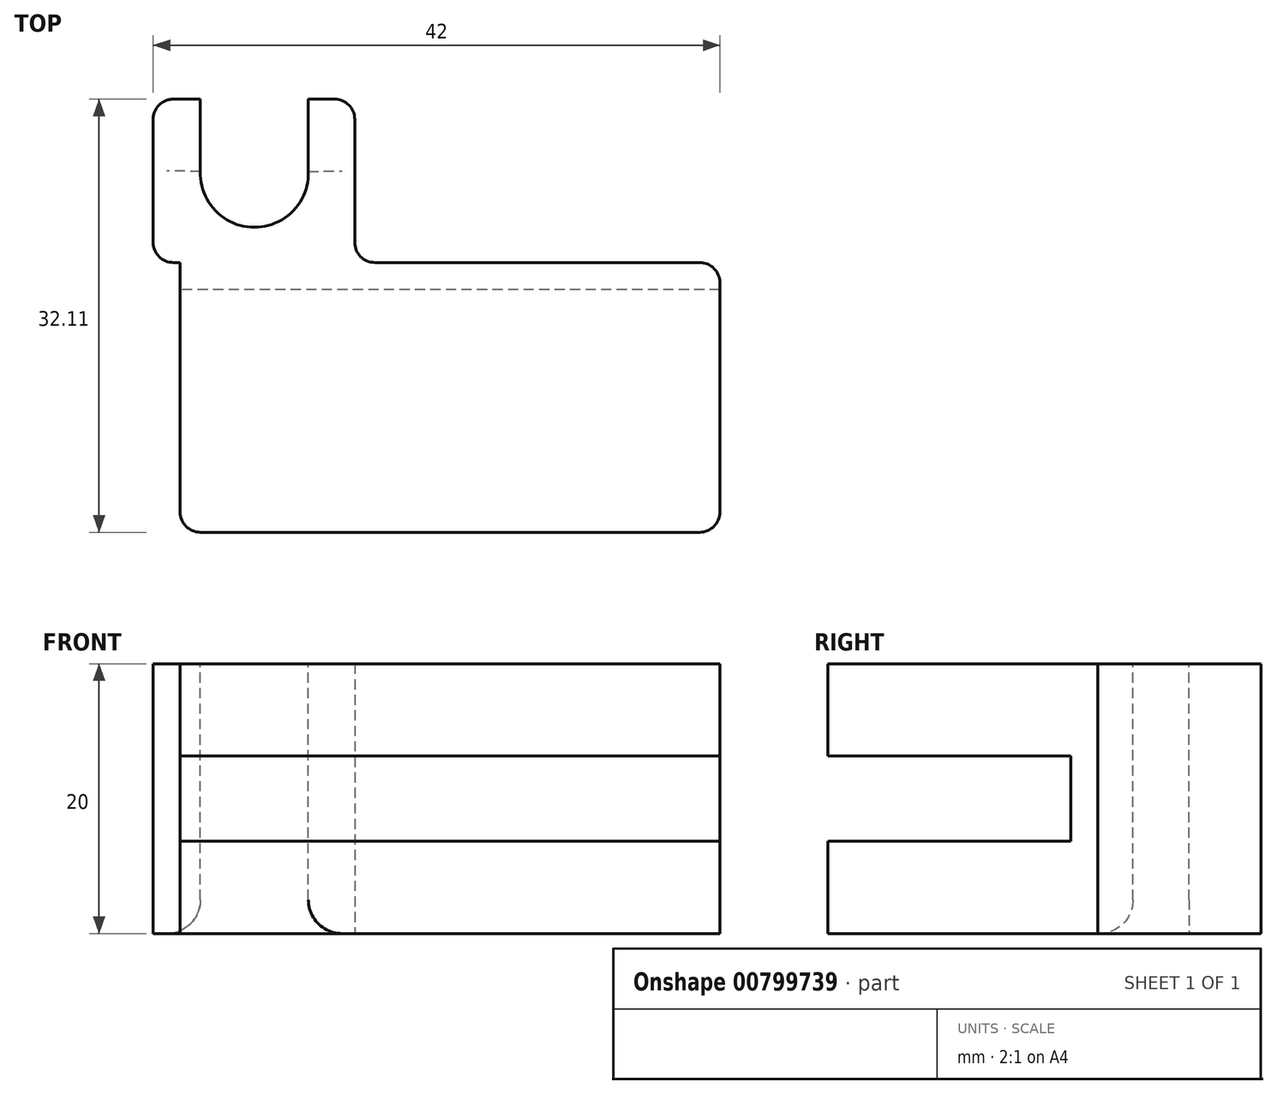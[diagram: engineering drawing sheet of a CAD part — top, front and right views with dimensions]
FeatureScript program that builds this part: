
annotation { "Feature Type Name" : "Feature", "Feature Type Description" : "" }
export const myFeature = defineFeature(function(context is Context, id is Id, definition is map)
    precondition{}
    {
        {
            var Q0;
            Q0=qCreatedBy(makeId("Top.planeOp"),FACE);
            var sketch = newSketch(context, id + "F0", { "sketchPlane" : qUnion([Q0])});
            skLineSegment(sketch, "E0.bottom", {"start": v(20, -10) * mm, "end": v(-20, -10) * mm});
            skLineSegment(sketch, "E0.top", {"start": v(20, 10) * mm, "end": v(-20, 10) * mm});
            skLineSegment(sketch, "E0.left", {"start": v(20, -10) * mm, "end": v(20, 10) * mm});
            skLineSegment(sketch, "E0.right", {"start": v(-20, -10) * mm, "end": v(-20, 10) * mm});
            skPoint(sketch, "E0.middle", {"position": v(0, 0) * mm});
            skPoint(sketch, "E1", {"position": v(-7.06, 10) * mm});
            skPoint(sketch, "E2", {"position": v(-7.06, 22.11) * mm});
            skPoint(sketch, "E3", {"position": v(-22, 22.11) * mm});
            skPoint(sketch, "E4", {"position": v(-22, 10) * mm});
            skLineSegment(sketch, "E5", {"start": v(-22, 10) * mm, "end": v(-20, 10) * mm});
            skLineSegment(sketch, "E6", {"start": v(-22, 22.11) * mm, "end": v(-22, 10) * mm});
            skLineSegment(sketch, "E7", {"start": v(-22, 22.11) * mm, "end": v(-7.06, 22.11) * mm});
            skLineSegment(sketch, "E8", {"start": v(-7.06, 22.11) * mm, "end": v(-7.06, 10) * mm});
            skSolve(sketch);
        }
        {
            var Q0;
            {var subQ0=sQuery(id+"F0.wireOp",EDGE,"E5");Q0=makeQuery(id+"F0.imprint","IMPRINT",FACE,{"disambiguationData":[TD([[makeQuery(id+"F0.imprint","IMPRINT",EDGE,{"derivedFrom":subQ0}),1.0]])]});}
            var Q1;
            Q1=makeQuery(id+"F0.imprint","IMPRINT",FACE,{"disambiguationData":[TD([[makeQuery(id+"F0.imprint","IMPRINT",EDGE,{"derivedFrom":sQuery(id+"F0.wireOp",EDGE,"E0.bottom")}),-1.0]])]});
            extrude(context, id + "F1", {"entities" : qUnion([Q0, Q1]), "depth" : 20 * mm, "offsetDistance" : 25 * mm});
        }
        {
            var Q0;
            Q0=makeQuery(id+"F1.opExtrude","CAP_FACE",FACE,{"disambiguationData":[OSD([sQuery(id+"F0.wireOp",EDGE,"E0.bottom"),sQuery(id+"F0.wireOp",EDGE,"E0.top"),sQuery(id+"F0.wireOp",EDGE,"E0.left"),sQuery(id+"F0.wireOp",EDGE,"E0.right"),sQuery(id+"F0.wireOp",EDGE,"E5"),sQuery(id+"F0.wireOp",EDGE,"E6"),sQuery(id+"F0.wireOp",EDGE,"E7"),sQuery(id+"F0.wireOp",EDGE,"E8")])],"isStart":false});
            var sketch = newSketch(context, id + "F2", { "sketchPlane" : qUnion([Q0])});
            skPoint(sketch, "E9", {"position": v(-14.5, 12.61) * mm});
            skPoint(sketch, "E10", {"position": v(-14.5, 16.61) * mm});
            skCircle(sketch, "E11", {"center": v(-14.5, 16.61) * mm, "radius": 4 * mm});
            skPoint(sketch, "E12", {"position": v(-10.5, 16.75) * mm});
            skPoint(sketch, "E13", {"position": v(-10.5, 22.11) * mm});
            skPoint(sketch, "E14", {"position": v(-18.5, 16.75) * mm});
            skPoint(sketch, "E15", {"position": v(-18.5, 22.11) * mm});
            skLineSegment(sketch, "E16", {"start": v(-18.5, 16.75) * mm, "end": v(-18.5, 22.11) * mm});
            skLineSegment(sketch, "E17", {"start": v(-10.5, 22.11) * mm, "end": v(-10.5, 16.75) * mm});
            skSolve(sketch);
        }
        {
            var Q0;
            {var subQ0=sQuery(id+"F2.wireOp",EDGE,"E11");var subQ1=makeQuery(id+"F2.imprint","INTERSECT",VERTEX,{"derivedFrom":[subQ0,sQuery(id+"F2.wireOp",EDGE,"E17")]});Q0=makeQuery(id+"F2.imprint","IMPRINT",FACE,{"disambiguationData":[TD([[makeQuery(id+"F2.imprint","IMPRINT",EDGE,{"disambiguationData":[TD([[subQ1,-1.0]])],"derivedFrom":subQ0}),1.0]])]});}
            var Q1;
            {var subQ0=sQuery(id+"F2.wireOp",EDGE,"E17");Q1=makeQuery(id+"F2.imprint","IMPRINT",FACE,{"disambiguationData":[TD([[makeQuery(id+"F2.imprint","IMPRINT",EDGE,{"derivedFrom":subQ0}),-1.0]])]});}
            var Q2;
            {var subQ0=sQuery(id+"F2.wireOp",EDGE,"E16");Q2=makeQuery(id+"F2.imprint","IMPRINT",FACE,{"disambiguationData":[TD([[makeQuery(id+"F2.imprint","IMPRINT",EDGE,{"derivedFrom":subQ0}),-1.0]])]});}
            extrude(context, id + "F3", {"entities" : qUnion([Q0, Q1, Q2]), "operationType" : NewBodyOperationType.REMOVE, "oppositeDirection" : true, "depth" : 25 * mm, "offsetDistance" : 25 * mm});
        }
        {
            var Q0;
            Q0=makeQuery(id+"F3.boolean.opBoolean","COPY",EDGE,{"derivedFrom":makeQuery(id+"F3.opExtrude","SWEPT_EDGE",EDGE,{"disambiguationData":[OSD([sQuery(id+"F0.wireOp",EDGE,"E7"),sQuery(id+"F2.wireOp",EDGE,"E16")])]})});
            var Q1;
            Q1=makeQuery(id+"F3.boolean.opBoolean","COPY",EDGE,{"derivedFrom":makeQuery(id+"F3.opExtrude","SWEPT_EDGE",EDGE,{"disambiguationData":[OSD([sQuery(id+"F0.wireOp",EDGE,"E7"),sQuery(id+"F2.wireOp",EDGE,"E17")])]})});
            var Q2;
            Q2=makeQuery(id+"F3.boolean.opBoolean","COPY",EDGE,{"derivedFrom":makeQuery(id+"F3.opExtrude","CAP_EDGE",EDGE,{"disambiguationData":[OSD([sQuery(id+"F2.wireOp",EDGE,"E11")])],"isStart":true})});
            var Q3;
            Q3=makeQuery(id+"F3.boolean.opBoolean","COPY",EDGE,{"derivedFrom":makeQuery(id+"F3.opExtrude","CAP_EDGE",EDGE,{"disambiguationData":[OSD([sQuery(id+"F2.wireOp",EDGE,"E16")])],"isStart":true})});
            var Q4;
            Q4=makeQuery(id+"F3.boolean.opBoolean","COPY",EDGE,{"derivedFrom":makeQuery(id+"F3.opExtrude","CAP_EDGE",EDGE,{"disambiguationData":[OSD([sQuery(id+"F2.wireOp",EDGE,"E17")])],"isStart":true})});
            var Q5;
            Q5=makeQuery(id+"F3.boolean.opBoolean","INTERSECT",EDGE,{"derivedFrom":[makeQuery(id+"F1.opExtrude","CAP_FACE",FACE,{"disambiguationData":[OSD([sQuery(id+"F0.wireOp",EDGE,"E0.bottom"),sQuery(id+"F0.wireOp",EDGE,"E0.top"),sQuery(id+"F0.wireOp",EDGE,"E0.left"),sQuery(id+"F0.wireOp",EDGE,"E0.right"),sQuery(id+"F0.wireOp",EDGE,"E5"),sQuery(id+"F0.wireOp",EDGE,"E6"),sQuery(id+"F0.wireOp",EDGE,"E7"),sQuery(id+"F0.wireOp",EDGE,"E8")])],"isStart":true}),makeQuery(id+"F3.opExtrude","SWEPT_FACE",FACE,{"disambiguationData":[OSD([sQuery(id+"F2.wireOp",EDGE,"E11")])]})]});
            var Q6;
            Q6=makeQuery(id+"F3.boolean.opBoolean","INTERSECT",EDGE,{"derivedFrom":[makeQuery(id+"F1.opExtrude","CAP_FACE",FACE,{"disambiguationData":[OSD([sQuery(id+"F0.wireOp",EDGE,"E0.bottom"),sQuery(id+"F0.wireOp",EDGE,"E0.top"),sQuery(id+"F0.wireOp",EDGE,"E0.left"),sQuery(id+"F0.wireOp",EDGE,"E0.right"),sQuery(id+"F0.wireOp",EDGE,"E5"),sQuery(id+"F0.wireOp",EDGE,"E6"),sQuery(id+"F0.wireOp",EDGE,"E7"),sQuery(id+"F0.wireOp",EDGE,"E8")])],"isStart":true}),makeQuery(id+"F3.opExtrude","SWEPT_FACE",FACE,{"disambiguationData":[OSD([sQuery(id+"F2.wireOp",EDGE,"E17")])]})]});
            var Q7;
            Q7=makeQuery(id+"F3.boolean.opBoolean","INTERSECT",EDGE,{"derivedFrom":[makeQuery(id+"F1.opExtrude","CAP_FACE",FACE,{"disambiguationData":[OSD([sQuery(id+"F0.wireOp",EDGE,"E0.bottom"),sQuery(id+"F0.wireOp",EDGE,"E0.top"),sQuery(id+"F0.wireOp",EDGE,"E0.left"),sQuery(id+"F0.wireOp",EDGE,"E0.right"),sQuery(id+"F0.wireOp",EDGE,"E5"),sQuery(id+"F0.wireOp",EDGE,"E6"),sQuery(id+"F0.wireOp",EDGE,"E7"),sQuery(id+"F0.wireOp",EDGE,"E8")])],"isStart":true}),makeQuery(id+"F3.opExtrude","SWEPT_FACE",FACE,{"disambiguationData":[OSD([sQuery(id+"F2.wireOp",EDGE,"E16")])]})]});
            fillet(context, id + "F4", {"entities" : qUnion([Q0, Q1, Q2, Q3, Q4, Q5, Q6, Q7]), "radius" : 2.5 * mm, "tangentPropagation" : true, "allowEdgeOverflow" : false});
        }
        {
            var Q0;
            Q0=makeQuery(id+"F1.opExtrude","SWEPT_FACE",FACE,{"disambiguationData":[OSD([sQuery(id+"F0.wireOp",EDGE,"E0.bottom")])]});
            var sketch = newSketch(context, id + "F5", { "sketchPlane" : qUnion([Q0])});
            skPoint(sketch, "E18", {"position": v(20, 0) * mm});
            skPoint(sketch, "E19", {"position": v(20, 20) * mm});
            skPoint(sketch, "E20", {"position": v(20, 13.15) * mm});
            skPoint(sketch, "E21", {"position": v(20, 6.85) * mm});
            skLineSegment(sketch, "E22", {"start": v(20, 13.15) * mm, "end": v(-20, 13.15) * mm});
            skLineSegment(sketch, "E23", {"start": v(20, 6.85) * mm, "end": v(-20, 6.85) * mm});
            skSolve(sketch);
        }
        {
            var Q0;
            {var subQ0=sQuery(id+"F5.wireOp",EDGE,"E22");Q0=makeQuery(id+"F5.imprint","IMPRINT",FACE,{"disambiguationData":[TD([[makeQuery(id+"F5.imprint","IMPRINT",EDGE,{"derivedFrom":subQ0}),1.0]])]});}
            extrude(context, id + "F6", {"entities" : qUnion([Q0]), "operationType" : NewBodyOperationType.REMOVE, "oppositeDirection" : true, "depth" : 18 * mm, "offsetDistance" : 25 * mm});
        }
        {
            var Q0;
            Q0=makeQuery(id+"F1.opExtrude","SWEPT_EDGE",EDGE,{"disambiguationData":[OSD([sQuery(id+"F0.wireOp",EDGE,"E6"),sQuery(id+"F0.wireOp",EDGE,"E7")])]});
            var Q1;
            Q1=makeQuery(id+"F1.opExtrude","SWEPT_EDGE",EDGE,{"disambiguationData":[OSD([sQuery(id+"F0.wireOp",EDGE,"E7"),sQuery(id+"F0.wireOp",EDGE,"E8")])]});
            var Q2;
            Q2=makeQuery(id+"F1.opExtrude","SWEPT_EDGE",EDGE,{"disambiguationData":[OSD([sQuery(id+"F0.wireOp",EDGE,"E0.top"),sQuery(id+"F0.wireOp",EDGE,"E8")])]});
            var Q3;
            Q3=makeQuery(id+"F1.opExtrude","SWEPT_EDGE",EDGE,{"disambiguationData":[OSD([sQuery(id+"F0.wireOp",EDGE,"E0.top"),sQuery(id+"F0.wireOp",EDGE,"E0.left")])]});
            var Q4;
            Q4=makeQuery(id+"F1.opExtrude","SWEPT_EDGE",EDGE,{"disambiguationData":[OSD([sQuery(id+"F0.wireOp",EDGE,"E5"),sQuery(id+"F0.wireOp",EDGE,"E6")])]});
            var Q5;
            {var subQ0=sQuery(id+"F0.wireOp",EDGE,"E0.bottom");var subQ1=sQuery(id+"F0.wireOp",EDGE,"E0.right");Q5=makeQuery(id+"F6.boolean.opBoolean","SPLIT",EDGE,{"disambiguationData":[TD([makeQuery(id+"F6.opExtrude","SWEPT_FACE",FACE,{"disambiguationData":[OSD([sQuery(id+"F5.wireOp",EDGE,"E23")])]})])],"derivedFrom":makeQuery(id+"F1.opExtrude","SWEPT_EDGE",EDGE,{"disambiguationData":[OSD([subQ0,subQ1])]})});}
            var Q6;
            {var subQ0=sQuery(id+"F0.wireOp",EDGE,"E0.bottom");var subQ1=sQuery(id+"F0.wireOp",EDGE,"E0.right");Q6=makeQuery(id+"F6.boolean.opBoolean","SPLIT",EDGE,{"disambiguationData":[TD([makeQuery(id+"F6.opExtrude","SWEPT_FACE",FACE,{"disambiguationData":[OSD([sQuery(id+"F5.wireOp",EDGE,"E22")])]})])],"derivedFrom":makeQuery(id+"F1.opExtrude","SWEPT_EDGE",EDGE,{"disambiguationData":[OSD([subQ0,subQ1])]})});}
            var Q7;
            {var subQ0=sQuery(id+"F0.wireOp",EDGE,"E0.bottom");var subQ1=sQuery(id+"F0.wireOp",EDGE,"E0.left");Q7=makeQuery(id+"F6.boolean.opBoolean","SPLIT",EDGE,{"disambiguationData":[TD([makeQuery(id+"F6.opExtrude","SWEPT_FACE",FACE,{"disambiguationData":[OSD([sQuery(id+"F5.wireOp",EDGE,"E22")])]})])],"derivedFrom":makeQuery(id+"F1.opExtrude","SWEPT_EDGE",EDGE,{"disambiguationData":[OSD([subQ0,subQ1])]})});}
            var Q8;
            {var subQ0=sQuery(id+"F0.wireOp",EDGE,"E0.bottom");var subQ1=sQuery(id+"F0.wireOp",EDGE,"E0.left");Q8=makeQuery(id+"F6.boolean.opBoolean","SPLIT",EDGE,{"disambiguationData":[TD([makeQuery(id+"F6.opExtrude","SWEPT_FACE",FACE,{"disambiguationData":[OSD([sQuery(id+"F5.wireOp",EDGE,"E23")])]})])],"derivedFrom":makeQuery(id+"F1.opExtrude","SWEPT_EDGE",EDGE,{"disambiguationData":[OSD([subQ0,subQ1])]})});}
            fillet(context, id + "F7", {"entities" : qUnion([Q0, Q1, Q2, Q3, Q4, Q5, Q6, Q7, Q8]), "radius" : 1.5 * mm, "tangentPropagation" : true, "allowEdgeOverflow" : false});
        }
    });
